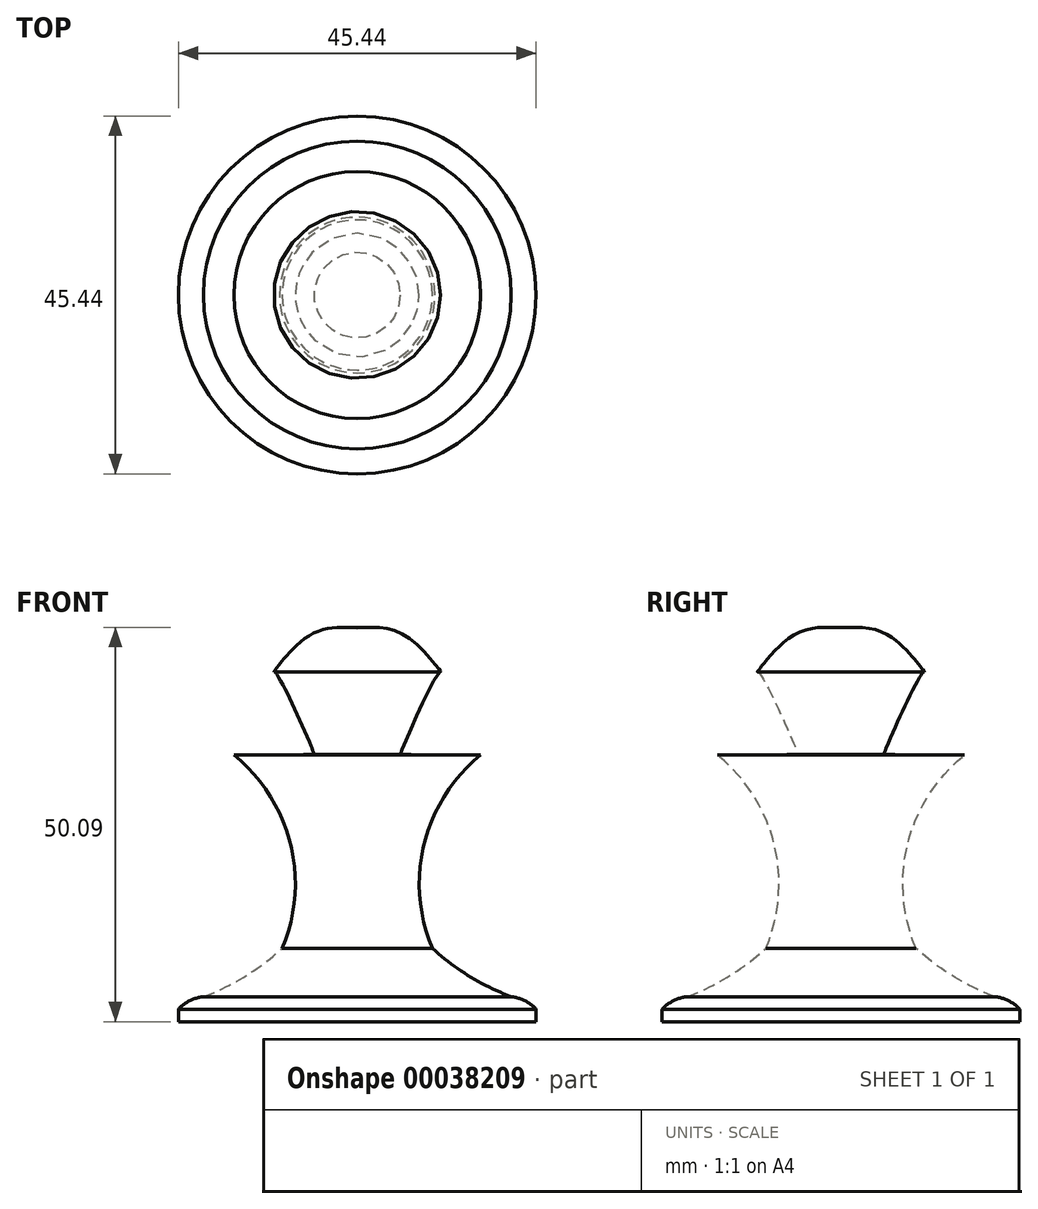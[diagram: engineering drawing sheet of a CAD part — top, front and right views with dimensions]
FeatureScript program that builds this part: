
annotation { "Feature Type Name" : "Feature", "Feature Type Description" : "" }
export const myFeature = defineFeature(function(context is Context, id is Id, definition is map)
    precondition{}
    {
        {
            var Q0;
            Q0=qCreatedBy(makeId("Front.planeOp"),FACE);
            var sketch = newSketch(context, id + "F0", { "sketchPlane" : qUnion([Q0])});
            skLineSegment(sketch, "E0", {"start": v(9.88, 11.42) * mm, "end": v(15.68, 11.42) * mm});
            skArc(sketch, "E1", {"start": v(15.68, 11.42) * mm, "mid": v(8.5, 0.18) * mm, "end": v(9.54, -13.12) * mm});
            skArc(sketch, "E2", {"start": v(9.54, -13.12) * mm, "mid": v(14.25, -16.68) * mm, "end": v(19.54, -19.26) * mm});
            skArc(sketch, "E3", {"start": v(22.72, -20.85) * mm, "mid": v(21.27, -19.78) * mm, "end": v(19.54, -19.26) * mm});
            skLineSegment(sketch, "E4", {"start": v(0, -22.44) * mm, "end": v(22.72, -22.44) * mm});
            skLineSegment(sketch, "E5", {"start": v(22.72, -20.85) * mm, "end": v(22.72, -22.44) * mm});
            skLineSegment(sketch, "E6", {"start": v(0, 27.56) * mm, "end": v(0, -22.44) * mm});
            skFitSpline(sketch, "E7", {"points": [v(0, 27.56) * mm, v(6.42, 26.39) * mm, v(10.6, 22) * mm, v(10.5, 22) * mm, v(5.46, 11.42) * mm, v(5.56, 11.42) * mm, v(9.88, 11.42) * mm], "startDerivative": vector(27.97, 1.98) * mm, "endDerivative": vector(31.11, -1.22) * mm});
            skSolve(sketch);
        }
        {
            var Q0;
            Q0=makeQuery(id+"F0.imprint","IMPRINT",FACE,{"disambiguationData":[TD([[makeQuery(id+"F0.imprint","IMPRINT",EDGE,{"derivedFrom":sQuery(id+"F0.wireOp",EDGE,"E0")}),-1.0]])]});
            var Q1;
            Q1=sQuery(id+"F0.wireOp",EDGE,"E6");
            revolve(context, id + "F1", {"entities" : qUnion([Q0]), "axis" : qUnion([Q1]), "revolveType" : RevolveType.FULL});
        }
    });
